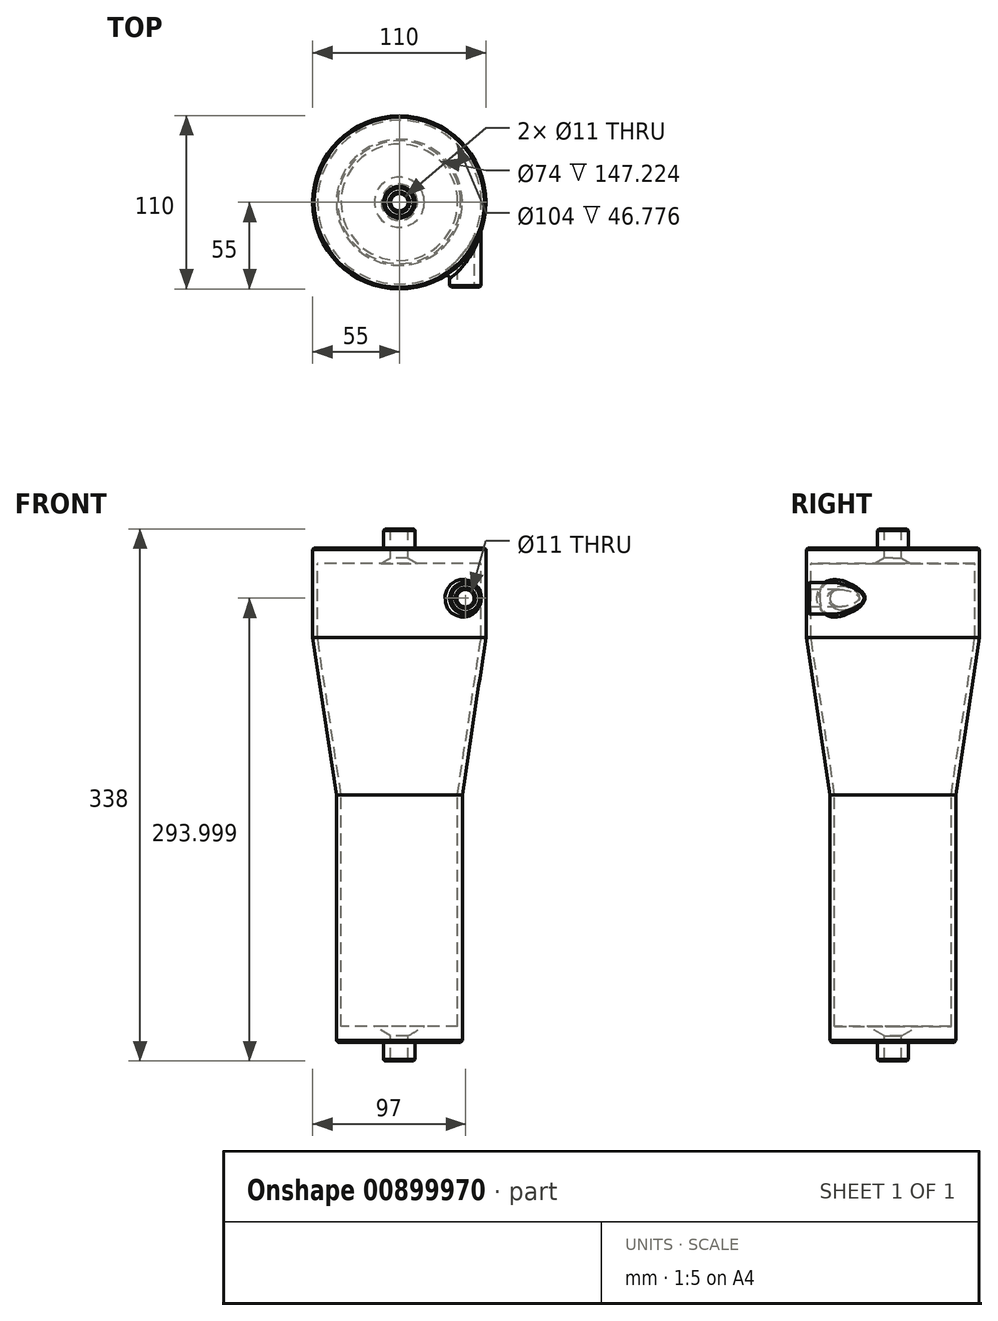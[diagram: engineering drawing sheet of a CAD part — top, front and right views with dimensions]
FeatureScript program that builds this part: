
annotation { "Feature Type Name" : "Feature", "Feature Type Description" : "" }
export const myFeature = defineFeature(function(context is Context, id is Id, definition is map)
    precondition{}
    {
        {
            var Q0;
            Q0=qCreatedBy(makeId("Front.planeOp"),FACE);
            var sketch = newSketch(context, id + "F0", { "sketchPlane" : qUnion([Q0])});
            skLineSegment(sketch, "E0", {"start": v(0, 51.74) * mm, "end": v(0, -66.22) * mm, "construction": true});
            skLineSegment(sketch, "E1", {"start": v(-5.5, 28.59) * mm, "end": v(-5.5, 50.59) * mm});
            skLineSegment(sketch, "E2", {"start": v(-5.5, 50.59) * mm, "end": v(-10, 50.59) * mm});
            skLineSegment(sketch, "E3", {"start": v(-10, 50.59) * mm, "end": v(-10, 38.59) * mm});
            skLineSegment(sketch, "E4", {"start": v(-10, 38.59) * mm, "end": v(-55, 38.59) * mm});
            skLineSegment(sketch, "E5", {"start": v(-55, 38.59) * mm, "end": v(-55, -18.41) * mm});
            skLineSegment(sketch, "E6", {"start": v(-55, -18.41) * mm, "end": v(-40, -118.41) * mm});
            skLineSegment(sketch, "E7", {"start": v(-40, -118.41) * mm, "end": v(-40, -275.41) * mm});
            skLineSegment(sketch, "E8", {"start": v(-40, -275.41) * mm, "end": v(-10, -275.41) * mm});
            skLineSegment(sketch, "E9", {"start": v(-10, -275.41) * mm, "end": v(-10, -287.41) * mm});
            skLineSegment(sketch, "E10", {"start": v(-10, -287.41) * mm, "end": v(-5.5, -287.41) * mm});
            skLineSegment(sketch, "E11", {"start": v(-5.5, -287.41) * mm, "end": v(-5.5, -265.41) * mm});
            skLineSegment(sketch, "E12", {"start": v(-5.5, -265.41) * mm, "end": v(-37, -265.41) * mm});
            skLineSegment(sketch, "E13", {"start": v(-37, -265.41) * mm, "end": v(-37, -118.19) * mm});
            skLineSegment(sketch, "E14", {"start": v(-37, -118.19) * mm, "end": v(-52, -18.19) * mm});
            skLineSegment(sketch, "E15", {"start": v(-52, -18.19) * mm, "end": v(-52, 28.59) * mm});
            skLineSegment(sketch, "E16", {"start": v(-52, 28.59) * mm, "end": v(-5.5, 28.59) * mm});
            skSolve(sketch);
        }
        {
            var Q0;
            Q0=makeQuery(id+"F0.imprint","IMPRINT",FACE,{"disambiguationData":[TD([[makeQuery(id+"F0.imprint","IMPRINT",EDGE,{"derivedFrom":sQuery(id+"F0.wireOp",EDGE,"E1")}),1.0]])]});
            var Q1;
            Q1=sQuery(id+"F0.wireOp",EDGE,"E0");
            revolve(context, id + "F1", {"surfaceOperationType" : NewSurfaceOperationType.NEW, "entities" : qUnion([Q0]), "axis" : qUnion([Q1]), "revolveType" : RevolveType.FULL});
        }
        {
            var Q0;
            Q0=makeQuery(id+"F1.opRevolve","SWEPT_EDGE",EDGE,{"disambiguationData":[OSD([sQuery(id+"F0.wireOp",EDGE,"E2"),sQuery(id+"F0.wireOp",EDGE,"E3")])]});
            var Q1;
            Q1=makeQuery(id+"F1.opRevolve","SWEPT_EDGE",EDGE,{"disambiguationData":[OSD([sQuery(id+"F0.wireOp",EDGE,"E4"),sQuery(id+"F0.wireOp",EDGE,"E5")])]});
            var Q2;
            Q2=makeQuery(id+"F1.opRevolve","SWEPT_EDGE",EDGE,{"disambiguationData":[OSD([sQuery(id+"F0.wireOp",EDGE,"E7"),sQuery(id+"F0.wireOp",EDGE,"E8")])]});
            var Q3;
            Q3=makeQuery(id+"F1.opRevolve","SWEPT_EDGE",EDGE,{"disambiguationData":[OSD([sQuery(id+"F0.wireOp",EDGE,"E9"),sQuery(id+"F0.wireOp",EDGE,"E10")])]});
            var Q4;
            Q4=makeQuery(id+"F1.opRevolve","SWEPT_EDGE",EDGE,{"disambiguationData":[OSD([sQuery(id+"F0.wireOp",EDGE,"E10"),sQuery(id+"F0.wireOp",EDGE,"E11")])]});
            var Q5;
            Q5=makeQuery(id+"F1.opRevolve","SWEPT_EDGE",EDGE,{"disambiguationData":[OSD([sQuery(id+"F0.wireOp",EDGE,"E1"),sQuery(id+"F0.wireOp",EDGE,"E2")])]});
            chamfer(context, id + "F2", {"entities" : qUnion([Q0, Q1, Q2, Q3, Q4, Q5]), "width" : 1 * mm, "tangentPropagation" : true});
        }
        {
            var Q0;
            Q0=makeQuery(id+"F1.opRevolve","SWEPT_EDGE",EDGE,{"disambiguationData":[OSD([sQuery(id+"F0.wireOp",EDGE,"E1"),sQuery(id+"F0.wireOp",EDGE,"E16")])]});
            chamfer(context, id + "F3", {"entities" : qUnion([Q0]), "chamferType" : ChamferType.OFFSET_ANGLE, "width" : 6 * mm, "oppositeDirection" : false, "angle" : 30 * degree, "tangentPropagation" : true});
        }
        {
            var Q0;
            Q0=makeQuery(id+"F1.opRevolve","SWEPT_EDGE",EDGE,{"disambiguationData":[OSD([sQuery(id+"F0.wireOp",EDGE,"E11"),sQuery(id+"F0.wireOp",EDGE,"E12")])]});
            chamfer(context, id + "F4", {"entities" : qUnion([Q0]), "chamferType" : ChamferType.OFFSET_ANGLE, "width" : 6 * mm, "oppositeDirection" : false, "angle" : 60 * degree, "tangentPropagation" : true});
        }
        {
            var Q0;
            Q0=makeQuery(id+"F1.opRevolve","SWEPT_FACE",FACE,{"disambiguationData":[OSD([sQuery(id+"F0.wireOp",EDGE,"E4")])]});
            cPlane(context, id + "F5", {"entities" : qUnion([Q0]), "cplaneType" : CPlaneType.OFFSET, "offset" : 32 * mm, "oppositeDirection" : true, "width" : 150 * mm, "height" : 150 * mm});
        }
        {
            var Q0;
            Q0=qCreatedBy(id+"F5.planeOp",FACE);
            var sketch = newSketch(context, id + "F6", { "sketchPlane" : qUnion([Q0])});
            skLineSegment(sketch, "E17", {"start": v(0, -24.94) * mm, "end": v(0, 58.56) * mm, "construction": true});
            skLineSegment(sketch, "E18.0", {"start": v(42, -58.5) * mm, "end": v(42, 58.56) * mm, "construction": true});
            skLineSegment(sketch, "E19", {"start": v(81.87, 0) * mm, "end": v(-28.44, 0) * mm, "construction": true});
            skLineSegment(sketch, "E20.0", {"start": v(52, -54) * mm, "end": v(47.5, -54) * mm});
            skLineSegment(sketch, "E21", {"start": v(52, -54) * mm, "end": v(52, -14) * mm});
            skLineSegment(sketch, "E22", {"start": v(52, -14) * mm, "end": v(50.08, -14) * mm});
            skLineSegment(sketch, "E23", {"start": v(47.5, -21.16) * mm, "end": v(47.5, -54) * mm});
            skCircle(sketch, "E24", {"center": v(0, 0) * mm, "radius": 52 * mm});
            skSolve(sketch);
        }
        {
            var Q0;
            Q0=makeQuery(id+"F6.imprint","IMPRINT",FACE,{"disambiguationData":[TD([[makeQuery(id+"F6.imprint","IMPRINT",EDGE,{"derivedFrom":sQuery(id+"F6.wireOp",EDGE,"E20.0")}),-1.0]])]});
            var Q1;
            Q1=sQuery(id+"F6.wireOp",EDGE,"E18.0");
            revolve(context, id + "F7", {"operationType" : NewBodyOperationType.ADD, "surfaceOperationType" : NewSurfaceOperationType.NEW, "entities" : qUnion([Q0]), "axis" : qUnion([Q1]), "revolveType" : RevolveType.FULL});
        }
        {
            var Q0;
            Q0=makeQuery(id+"F7.opRevolve","SWEPT_EDGE",EDGE,{"disambiguationData":[OSD([sQuery(id+"F6.wireOp",EDGE,"E20.0"),sQuery(id+"F6.wireOp",EDGE,"E21")])]});
            var Q1;
            Q1=makeQuery(id+"F7.opRevolve","SWEPT_EDGE",EDGE,{"disambiguationData":[OSD([sQuery(id+"F6.wireOp",EDGE,"E20.0"),sQuery(id+"F6.wireOp",EDGE,"E23")])]});
            chamfer(context, id + "F8", {"entities" : qUnion([Q0, Q1]), "width" : 1 * mm, "tangentPropagation" : true});
        }
        {
            var Q0;
            Q0=makeQuery(id+"F7.boolean.opBoolean","INTERSECT",EDGE,{"derivedFrom":[makeQuery(id+"F1.opRevolve","SWEPT_FACE",FACE,{"disambiguationData":[OSD([sQuery(id+"F0.wireOp",EDGE,"E5")])]}),makeQuery(id+"F7.opRevolve","SWEPT_FACE",FACE,{"disambiguationData":[OSD([sQuery(id+"F6.wireOp",EDGE,"E21")])]})]});
            fillet(context, id + "F9", {"entities" : qUnion([Q0]), "radius" : 2 * mm, "tangentPropagation" : true, "allowEdgeOverflow" : false});
        }
        {
            var Q0;
            {var subQ0=sQuery(id+"F6.wireOp",EDGE,"E24");var subQ1=makeQuery(id+"F6.imprint","INTERSECT",VERTEX,{"derivedFrom":[sQuery(id+"F6.wireOp",EDGE,"E22"),subQ0]});Q0=makeQuery(id+"F6.imprint","IMPRINT",FACE,{"disambiguationData":[TD([[makeQuery(id+"F6.imprint","IMPRINT",EDGE,{"disambiguationData":[TD([[subQ1,1.0]])],"derivedFrom":subQ0}),1.0]])]});}
            extrude(context, id + "F10", {"entities" : qUnion([Q0]), "operationType" : NewBodyOperationType.REMOVE, "endBound" : BoundingType.SYMMETRIC, "depth" : 25 * mm, "offsetDistance" : 25 * mm});
        }
        {
            var Q0;
            Q0=makeQuery(id+"F7.opRevolve","SWEPT_FACE",FACE,{"disambiguationData":[OSD([sQuery(id+"F6.wireOp",EDGE,"E20.0")])]});
            var sketch = newSketch(context, id + "F11", { "sketchPlane" : qUnion([Q0])});
            skCircle(sketch, "E25", {"center": v(42, 6.59) * mm, "radius": 5.5 * mm});
            skSolve(sketch);
        }
        {
            var Q0;
            Q0=makeQuery(id+"F11.imprint","IMPRINT",FACE,{"disambiguationData":[TD([[makeQuery(id+"F11.imprint","IMPRINT",EDGE,{"derivedFrom":sQuery(id+"F11.wireOp",EDGE,"E25")}),1.0]])]});
            extrude(context, id + "F12", {"entities" : qUnion([Q0]), "operationType" : NewBodyOperationType.REMOVE, "oppositeDirection" : true, "depth" : 40 * mm, "offsetDistance" : 25 * mm});
        }
        {
            var Q0;
            {var subQ0=sQuery(id+"F6.wireOp",EDGE,"E24");var subQ2=makeQuery(id+"F1.opRevolve","SWEPT_FACE",FACE,{"disambiguationData":[OSD([sQuery(id+"F0.wireOp",EDGE,"E15")])]});Q0=makeQuery(id+"F12.boolean.opBoolean","INTERSECT",EDGE,{"derivedFrom":[makeQuery(id+"F10.boolean.opBoolean","MERGE",FACE,{"derivedFrom":[makeQuery(id+"F7.boolean.opBoolean","SPLIT",FACE,{"disambiguationData":[TD([makeQuery(id+"F7.opRevolve","SWEPT_FACE",FACE,{"disambiguationData":[OSD([sQuery(id+"F6.wireOp",EDGE,"E23")])]})])],"derivedFrom":subQ2}),makeQuery(id+"F7.boolean.opBoolean","SPLIT",FACE,{"disambiguationData":[TD([makeQuery(id+"F1.opRevolve","SWEPT_FACE",FACE,{"disambiguationData":[OSD([sQuery(id+"F0.wireOp",EDGE,"E14")])]})])],"derivedFrom":subQ2})],"fromTools":[makeQuery(id+"F10.opExtrude","SWEPT_FACE",FACE,{"disambiguationData":[OSD([subQ0])]})]}),makeQuery(id+"F12.opExtrude","SWEPT_FACE",FACE,{"disambiguationData":[OSD([sQuery(id+"F11.wireOp",EDGE,"E25")])]})]});}
            fillet(context, id + "F13", {"entities" : qUnion([Q0]), "radius" : 2 * mm, "tangentPropagation" : true, "allowEdgeOverflow" : false});
        }
    });
